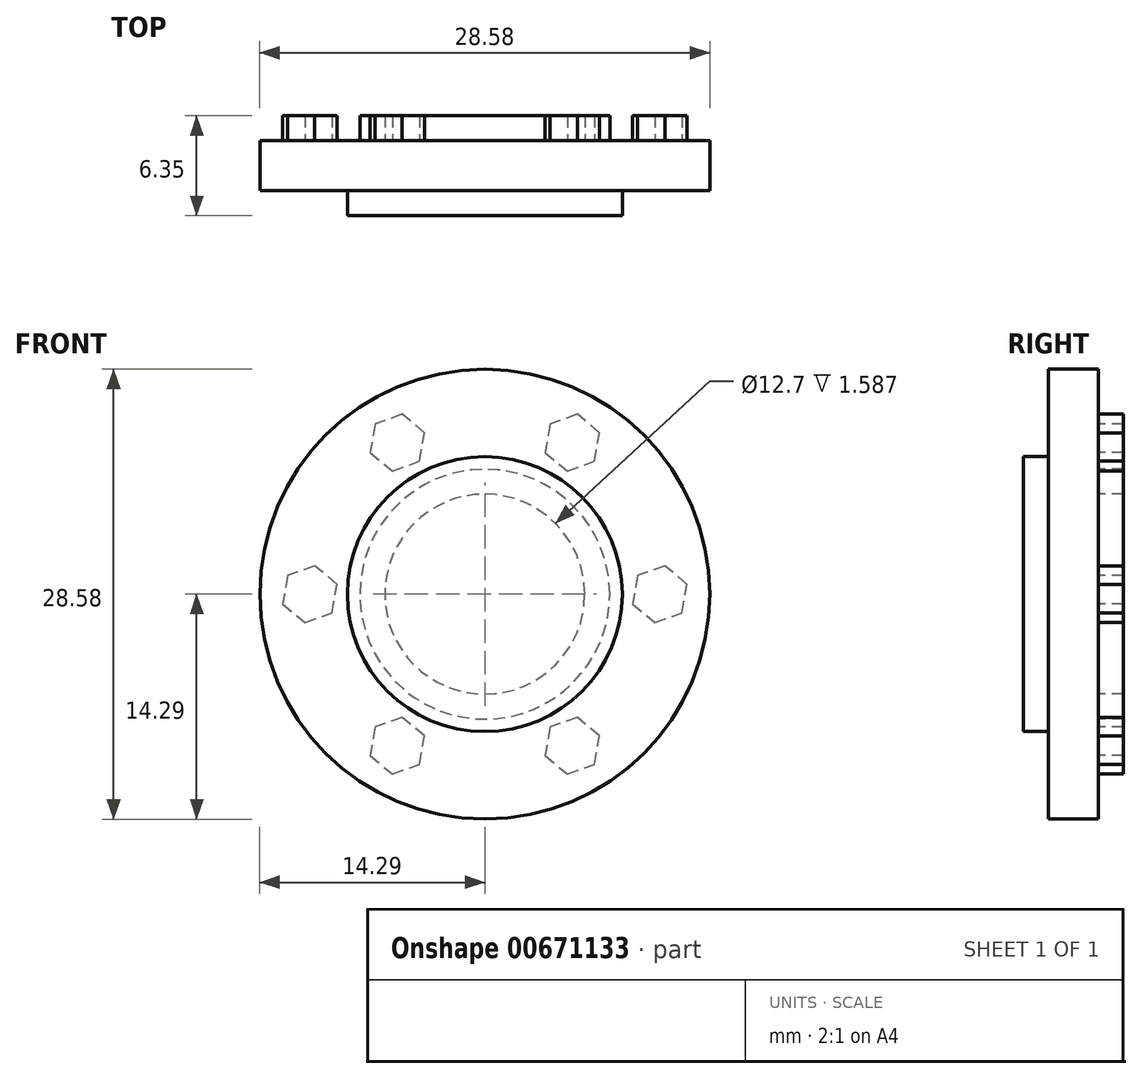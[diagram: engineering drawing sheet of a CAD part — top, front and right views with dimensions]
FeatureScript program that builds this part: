
annotation { "Feature Type Name" : "Feature", "Feature Type Description" : "" }
export const myFeature = defineFeature(function(context is Context, id is Id, definition is map)
    precondition{}
    {
        {
            var Q0;
            Q0=qCreatedBy(makeId("Front.planeOp"),FACE);
            var sketch = newSketch(context, id + "F0", { "sketchPlane" : qUnion([Q0])});
            skCircle(sketch, "E0", {"center": v(0, 0) * mm, "radius": 14.29 * mm});
            skSolve(sketch);
        }
        {
            var Q0;
            Q0=qSketchRegion(id+"F0",true);
            extrude(context, id + "F1", {"entities" : qUnion([Q0]), "depth" : 3.17 * mm});
        }
        {
            var Q0;
            Q0=makeQuery(id+"F1.opExtrude","CAP_FACE",FACE,{"disambiguationData":[OSD([sQuery(id+"F0.wireOp",EDGE,"E0")])],"isStart":false});
            var sketch = newSketch(context, id + "F2", { "sketchPlane" : qUnion([Q0])});
            skCircle(sketch, "E1", {"center": v(0, 0) * mm, "radius": 8.73 * mm});
            skSolve(sketch);
        }
        {
            var Q0;
            Q0=qSketchRegion(id+"F2",true);
            extrude(context, id + "F3", {"entities" : qUnion([Q0]), "operationType" : NewBodyOperationType.ADD, "depth" : 1.59 * mm});
        }
        {
            var Q0;
            Q0=makeQuery(id+"F1.opExtrude","CAP_FACE",FACE,{"disambiguationData":[OSD([sQuery(id+"F0.wireOp",EDGE,"E0")])],"isStart":true});
            var sketch = newSketch(context, id + "F4", { "sketchPlane" : qUnion([Q0])});
            skCircle(sketch, "E2.cCircle", {"center": v(11.11, 0) * mm, "radius": 1.59 * mm, "construction": true});
            skLineSegment(sketch, "E2.0", {"start": v(12.83, -0.63) * mm, "end": v(11.43, -1.8) * mm});
            skLineSegment(sketch, "E2.1", {"start": v(11.43, -1.8) * mm, "end": v(9.7, -1.18) * mm});
            skLineSegment(sketch, "E2.2", {"start": v(9.7, -1.18) * mm, "end": v(9.4, 0.63) * mm});
            skLineSegment(sketch, "E2.3", {"start": v(9.4, 0.63) * mm, "end": v(10.8, 1.8) * mm});
            skLineSegment(sketch, "E2.4", {"start": v(10.8, 1.8) * mm, "end": v(12.52, 1.18) * mm});
            skLineSegment(sketch, "E2.5", {"start": v(12.52, 1.18) * mm, "end": v(12.83, -0.63) * mm});
            skPoint(sketch, "E2.0.midPoint", {"position": v(12.13, -1.22) * mm});
            skSolve(sketch);
        }
        {
            var Q0;
            Q0=qSketchRegion(id+"F4",true);
            extrude(context, id + "F5", {"entities" : qUnion([Q0]), "depth" : 1.59 * mm});
        }
        {
            var Q0;
            Q0=makeQuery(id+"F1.opExtrude","CAP_FACE",FACE,{"disambiguationData":[OSD([sQuery(id+"F0.wireOp",EDGE,"E0")])],"isStart":true});
            var sketch = newSketch(context, id + "F6", { "sketchPlane" : qUnion([Q0])});
            skCircle(sketch, "E3", {"center": v(0, 0) * mm, "radius": 7.94 * mm});
            skCircle(sketch, "E4", {"center": v(0, 0) * mm, "radius": 6.35 * mm});
            skSolve(sketch);
        }
        {
            var Q0;
            Q0=qSketchRegion(id+"F6",true);
            extrude(context, id + "F7", {"entities" : qUnion([Q0]), "operationType" : NewBodyOperationType.ADD, "depth" : 1.59 * mm});
        }
        {
            var Q0;
            Q0=makeQuery(id+"F5.opExtrude","SWEPT_BODY",BODY,{"disambiguationData":[OSD([sQuery(id+"F4.wireOp",EDGE,"E2.0"),sQuery(id+"F4.wireOp",EDGE,"E2.1"),sQuery(id+"F4.wireOp",EDGE,"E2.2"),sQuery(id+"F4.wireOp",EDGE,"E2.3"),sQuery(id+"F4.wireOp",EDGE,"E2.4"),sQuery(id+"F4.wireOp",EDGE,"E2.5")])]});
            var Q1;
            Q1=makeQuery(id+"F7.opExtrude","CAP_EDGE",EDGE,{"disambiguationData":[OSD([sQuery(id+"F6.wireOp",EDGE,"E4")])],"isStart":false});
            circularPattern(context, id + "F8", {"entities" : qUnion([Q0]), "axis" : qUnion([Q1]), "angle" : 360 * degree, "instanceCount" : 6, "equalSpace" : true});
        }
    });
